# Revit family: Toilet-Floor_Mount-KOHLER-Veil-K-28161
name_source: partatom
category: Plumbing Fixtures
units: mm (PartAtom-declared; Revit-internal decimal feet)

## family parameters
Cut with Voids When Loaded = No
Host = Face
OmniClass Number = 23.31.19.00
OmniClass Title = Toilets
Part Type = Normal
Room Calculation Point = No
Round Connector Dimension = Use Diameter
Shared = No

## types (3) — shared parameters
ADA Compliant = No
Apparent Load = 1800 VA
Assembly Code = D2010100
Bowl Height = 16 1/2"
CW Connection = Yes
Cold Water Inlet = Cold Water Inlet
Date Modified = 10/02/2024
Default Elevation = 0"
Description = Comfort Height Elongated Bowl 1.28 Two Piece Toilet Hidden Cord
Electrical Connector = Yes
Electrical Note = One Dedicated Circuit Required
Flow Rate = 0 GPM
Flush Rate- GPF = GPF
Flush Rate- LPF = LPF
HW Connection = No
Height = 31"
Hot Water Inlet = Hot Water Inlet
Length = 28 1/4"
Manufacturer = Kohler Co.
Master Format 2014 = 22 42 13.13
Master Format 2014 Name = Residential Water Closets
Material = Vitreous China
Pressure = 0.00 psi
Product Documentation Link = https://www.us.kohler.com
Product Name = Veil
Product Page URL = http://www.us.kohler.com
Rough In = 12"
Seat Included = No
URL = https://www.us.kohler.com
Vent Connection = No
Voltage = 120 V
Waste Connection = Yes
Waste Water Outlet = Waste Water Outlet
WaterSense Certified = No
Width = 15"

## per-type parameters (varying)
| type | Finish | Model | Type |
| 0-White | Kohler-Vitreous_China-0-White | K-28161-HC-0 | 1 |
| 7-Black Black | Kohler-Vitreous_China-7-Black_Black | K-28161-HC-7 | 2 |
| 96-Biscuit | Kohler-Vitreous_China-96-Biscuit | K-28161-HC-96 | 3 |

## geometry (parser evidence)
native form markers: Sweep x11
no freeform markers — native parametric forms only
